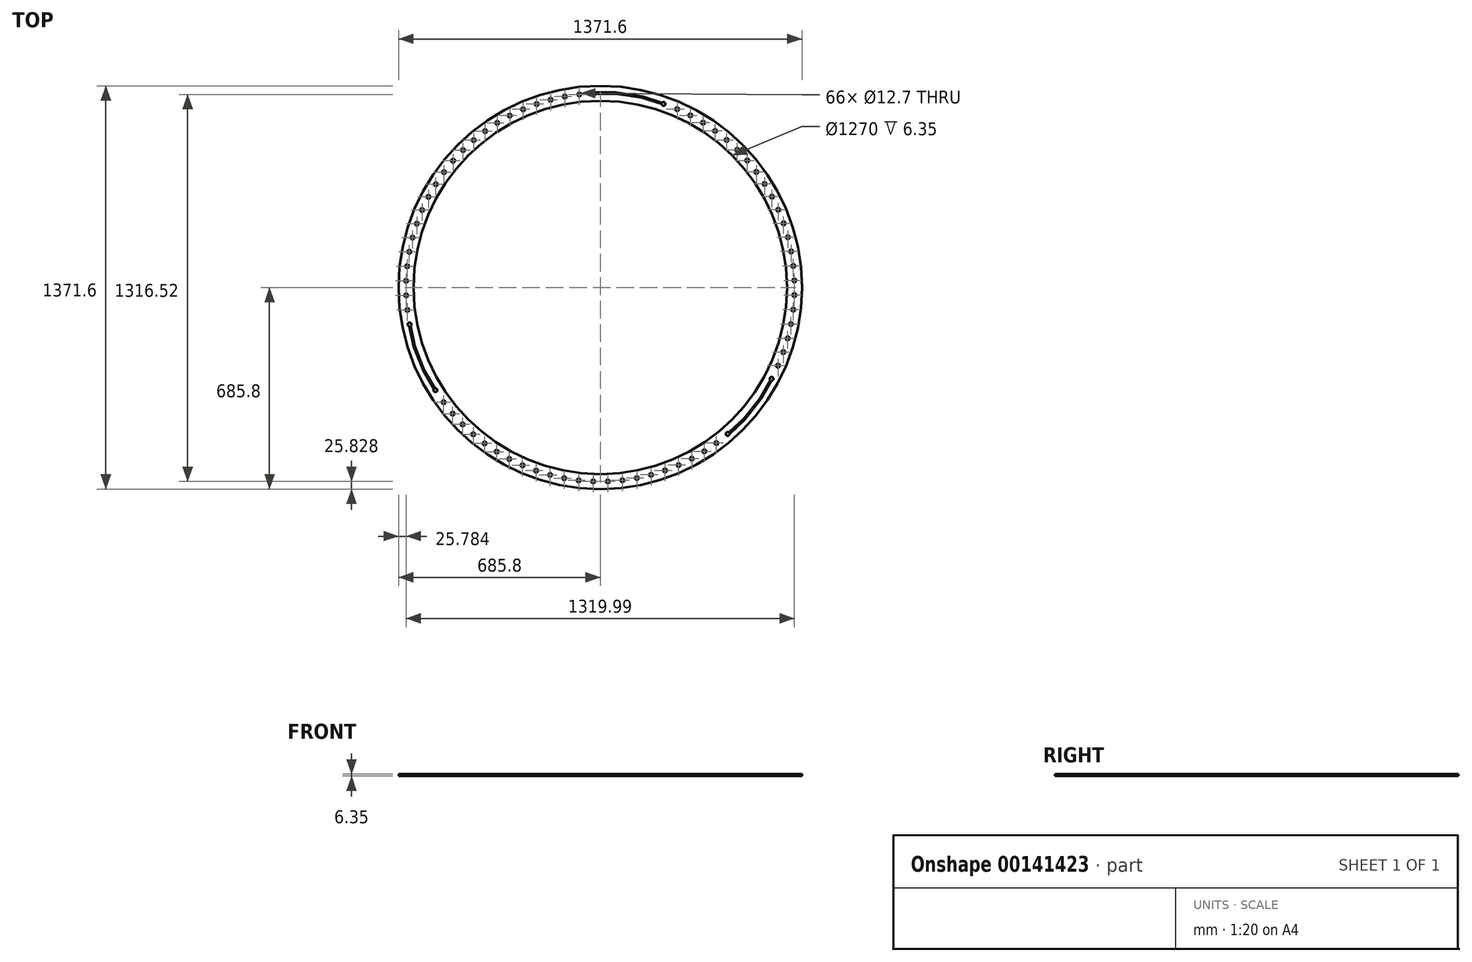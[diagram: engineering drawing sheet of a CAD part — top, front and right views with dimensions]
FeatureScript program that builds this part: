
annotation { "Feature Type Name" : "Feature", "Feature Type Description" : "" }
export const myFeature = defineFeature(function(context is Context, id is Id, definition is map)
    precondition{}
    {
        {
            var Q0;
            Q0=qCreatedBy(makeId("Top.planeOp"),FACE);
            var sketch = newSketch(context, id + "F0", { "sketchPlane" : qUnion([Q0])});
            skCircle(sketch, "E0", {"center": v(0, 0) * mm, "radius": 685.8 * mm});
            skCircle(sketch, "E1", {"center": v(0, 0) * mm, "radius": 635 * mm});
            skCircle(sketch, "E2", {"center": v(-560.48, -349.27) * mm, "radius": 6.35 * mm});
            skCircle(sketch, "E3", {"center": v(-532.66, -390.39) * mm, "radius": 6.35 * mm});
            skCircle(sketch, "E4", {"center": v(-501.83, -429.3) * mm, "radius": 6.35 * mm});
            skCircle(sketch, "E5", {"center": v(-468.16, -465.78) * mm, "radius": 6.35 * mm});
            skCircle(sketch, "E6", {"center": v(-431.84, -499.64) * mm, "radius": 6.35 * mm});
            skCircle(sketch, "E7", {"center": v(-393.09, -530.67) * mm, "radius": 6.35 * mm});
            skCircle(sketch, "E8", {"center": v(-352.11, -558.7) * mm, "radius": 6.35 * mm});
            skCircle(sketch, "E9", {"center": v(-309.15, -583.57) * mm, "radius": 6.35 * mm});
            skCircle(sketch, "E10", {"center": v(-264.43, -605.15) * mm, "radius": 6.35 * mm});
            skCircle(sketch, "E11", {"center": v(-218.23, -623.3) * mm, "radius": 6.35 * mm});
            skCircle(sketch, "E12", {"center": v(-170.8, -637.93) * mm, "radius": 6.35 * mm});
            skCircle(sketch, "E13", {"center": v(-122.39, -648.96) * mm, "radius": 6.35 * mm});
            skCircle(sketch, "E14", {"center": v(-73.3, -656.32) * mm, "radius": 6.35 * mm});
            skCircle(sketch, "E15", {"center": v(-23.78, -659.97) * mm, "radius": 6.35 * mm});
            skCircle(sketch, "E16", {"center": v(25.86, -659.9) * mm, "radius": 6.35 * mm});
            skCircle(sketch, "E17", {"center": v(75.36, -656.09) * mm, "radius": 6.35 * mm});
            skCircle(sketch, "E18", {"center": v(124.43, -648.57) * mm, "radius": 6.35 * mm});
            skCircle(sketch, "E19", {"center": v(172.8, -637.4) * mm, "radius": 6.35 * mm});
            skCircle(sketch, "E20", {"center": v(220.2, -622.6) * mm, "radius": 6.35 * mm});
            skCircle(sketch, "E21", {"center": v(266.34, -604.3) * mm, "radius": 6.35 * mm});
            skCircle(sketch, "E22", {"center": v(310.99, -582.6) * mm, "radius": 6.35 * mm});
            skCircle(sketch, "E23", {"center": v(353.87, -557.59) * mm, "radius": 6.35 * mm});
            skCircle(sketch, "E24", {"center": v(582.66, -310.87) * mm, "radius": 6.35 * mm});
            skCircle(sketch, "E25", {"center": v(604.36, -266.22) * mm, "radius": 6.35 * mm});
            skCircle(sketch, "E26", {"center": v(622.65, -220.07) * mm, "radius": 6.35 * mm});
            skCircle(sketch, "E27", {"center": v(637.36, -172.91) * mm, "radius": 6.35 * mm});
            skCircle(sketch, "E28", {"center": v(648.55, -124.54) * mm, "radius": 6.35 * mm});
            skCircle(sketch, "E29", {"center": v(656.07, -75.47) * mm, "radius": 6.35 * mm});
            skCircle(sketch, "E30", {"center": v(659.89, -25.98) * mm, "radius": 6.35 * mm});
            skCircle(sketch, "E31", {"center": v(659.98, 23.67) * mm, "radius": 6.35 * mm});
            skCircle(sketch, "E32", {"center": v(656.33, 73.18) * mm, "radius": 6.35 * mm});
            skCircle(sketch, "E33", {"center": v(648.98, 122.28) * mm, "radius": 6.35 * mm});
            skCircle(sketch, "E34", {"center": v(637.96, 170.68) * mm, "radius": 6.35 * mm});
            skCircle(sketch, "E35", {"center": v(623.34, 218.12) * mm, "radius": 6.35 * mm});
            skCircle(sketch, "E36", {"center": v(605.2, 264.33) * mm, "radius": 6.35 * mm});
            skCircle(sketch, "E37", {"center": v(583.62, 309.05) * mm, "radius": 6.35 * mm});
            skCircle(sketch, "E38", {"center": v(558.76, 352.02) * mm, "radius": 6.35 * mm});
            skCircle(sketch, "E39", {"center": v(530.74, 393) * mm, "radius": 6.35 * mm});
            skCircle(sketch, "E40", {"center": v(499.72, 431.75) * mm, "radius": 6.35 * mm});
            skCircle(sketch, "E41", {"center": v(465.87, 468.07) * mm, "radius": 6.35 * mm});
            skCircle(sketch, "E42", {"center": v(429.4, 501.75) * mm, "radius": 6.35 * mm});
            skCircle(sketch, "E43", {"center": v(390.49, 532.58) * mm, "radius": 6.35 * mm});
            skCircle(sketch, "E44", {"center": v(349.38, 560.41) * mm, "radius": 6.35 * mm});
            skCircle(sketch, "E45", {"center": v(306.3, 585.08) * mm, "radius": 6.35 * mm});
            skCircle(sketch, "E46", {"center": v(-71.24, 656.55) * mm, "radius": 6.35 * mm});
            skCircle(sketch, "E47", {"center": v(-120.36, 649.34) * mm, "radius": 6.35 * mm});
            skCircle(sketch, "E48", {"center": v(-168.8, 638.46) * mm, "radius": 6.35 * mm});
            skCircle(sketch, "E49", {"center": v(-216.28, 623.98) * mm, "radius": 6.35 * mm});
            skCircle(sketch, "E50", {"center": v(-262.54, 605.97) * mm, "radius": 6.35 * mm});
            skCircle(sketch, "E51", {"center": v(-307.32, 584.54) * mm, "radius": 6.35 * mm});
            skCircle(sketch, "E52", {"center": v(-350.36, 559.8) * mm, "radius": 6.35 * mm});
            skCircle(sketch, "E53", {"center": v(-391.42, 531.9) * mm, "radius": 6.35 * mm});
            skCircle(sketch, "E54", {"center": v(-430.28, 501) * mm, "radius": 6.35 * mm});
            skCircle(sketch, "E55", {"center": v(-466.7, 467.25) * mm, "radius": 6.35 * mm});
            skCircle(sketch, "E56", {"center": v(-500.48, 430.87) * mm, "radius": 6.35 * mm});
            skCircle(sketch, "E57", {"center": v(-531.43, 392.06) * mm, "radius": 6.35 * mm});
            skCircle(sketch, "E58", {"center": v(-559.38, 351.03) * mm, "radius": 6.35 * mm});
            skCircle(sketch, "E59", {"center": v(-584.17, 308.02) * mm, "radius": 6.35 * mm});
            skCircle(sketch, "E60", {"center": v(-605.66, 263.27) * mm, "radius": 6.35 * mm});
            skCircle(sketch, "E61", {"center": v(-623.72, 217.03) * mm, "radius": 6.35 * mm});
            skCircle(sketch, "E62", {"center": v(-638.26, 169.56) * mm, "radius": 6.35 * mm});
            skCircle(sketch, "E63", {"center": v(-649.2, 121.13) * mm, "radius": 6.35 * mm});
            skCircle(sketch, "E64", {"center": v(-656.46, 72.02) * mm, "radius": 6.35 * mm});
            skCircle(sketch, "E65", {"center": v(-660.02, 22.5) * mm, "radius": 6.35 * mm});
            skCircle(sketch, "E66", {"center": v(-659.84, -27.14) * mm, "radius": 6.35 * mm});
            skCircle(sketch, "E67", {"center": v(-655.94, -76.63) * mm, "radius": 6.35 * mm});
            skCircle(sketch, "E68", {"center": v(-648.33, -125.68) * mm, "radius": 6.35 * mm});
            skCircle(sketch, "E69", {"center": v(394.76, -529.43) * mm, "radius": 6.35 * mm});
            skCircle(sketch, "E70", {"center": v(261.48, 606.43) * mm, "radius": 6.35 * mm});
            skCircle(sketch, "E71", {"center": v(-21.72, 660.04) * mm, "radius": 6.35 * mm});
            skCircle(sketch, "E72", {"center": v(433.41, -498.28) * mm, "radius": 6.35 * mm});
            skCircle(sketch, "E73", {"center": v(215.18, 624.36) * mm, "radius": 6.35 * mm});
            skLineSegment(sketch, "E74", {"start": v(-649.95, -131.2) * mm, "end": v(-634.75, -201) * mm});
            skLineSegment(sketch, "E75", {"start": v(-634.75, -201) * mm, "end": v(-601.96, -284.24) * mm});
            skLineSegment(sketch, "E76", {"start": v(-601.96, -284.24) * mm, "end": v(-565.83, -345.85) * mm});
            skLineSegment(sketch, "E77", {"start": v(-645.19, -131.2) * mm, "end": v(-630.64, -198.57) * mm});
            skLineSegment(sketch, "E78", {"start": v(-630.64, -198.57) * mm, "end": v(-598.5, -280.94) * mm});
            skLineSegment(sketch, "E79", {"start": v(-598.5, -280.94) * mm, "end": v(-561.93, -343.09) * mm});
            skLineSegment(sketch, "E80", {"start": v(439.76, -498.28) * mm, "end": v(491.73, -449.04) * mm});
            skLineSegment(sketch, "E81", {"start": v(491.73, -449.04) * mm, "end": v(547.19, -379.02) * mm});
            skLineSegment(sketch, "E82", {"start": v(582.66, -317.22) * mm, "end": v(547.19, -379.02) * mm});
            skLineSegment(sketch, "E83", {"start": v(437.97, -493.85) * mm, "end": v(487.9, -446.19) * mm});
            skLineSegment(sketch, "E84", {"start": v(578.33, -315.52) * mm, "end": v(542.56, -377.84) * mm});
            skLineSegment(sketch, "E85", {"start": v(542.56, -377.84) * mm, "end": v(487.9, -446.19) * mm});
            skLineSegment(sketch, "E86", {"start": v(-16.55, 663.74) * mm, "end": v(53.38, 663.74) * mm});
            skLineSegment(sketch, "E87", {"start": v(141.78, 650.6) * mm, "end": v(210.53, 628.68) * mm});
            skLineSegment(sketch, "E88", {"start": v(53.38, 663.74) * mm, "end": v(144.29, 649.8) * mm});
            skLineSegment(sketch, "E89", {"start": v(-15.44, 659.1) * mm, "end": v(52.27, 659.1) * mm});
            skLineSegment(sketch, "E90", {"start": v(52.27, 659.1) * mm, "end": v(139.95, 646.18) * mm});
            skLineSegment(sketch, "E91", {"start": v(139.95, 646.18) * mm, "end": v(208.83, 624.21) * mm});
            skSolve(sketch);
        }
        {
            var Q0;
            Q0=makeQuery(id+"F0.imprint","IMPRINT",FACE,{"disambiguationData":[TD([[makeQuery(id+"F0.imprint","IMPRINT",EDGE,{"derivedFrom":sQuery(id+"F0.wireOp",EDGE,"E0")}),1.0]])]});
            extrude(context, id + "F1", {"entities" : qUnion([Q0]), "depth" : 6.35 * mm});
        }
    });
